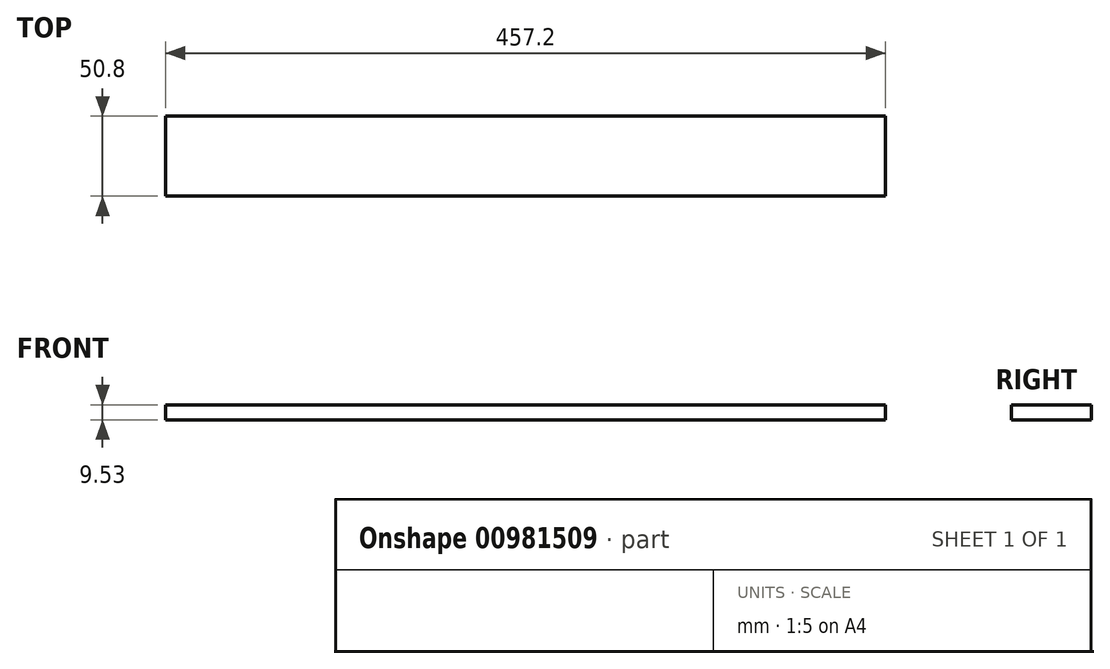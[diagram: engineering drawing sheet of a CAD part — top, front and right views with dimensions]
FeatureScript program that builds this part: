
annotation { "Feature Type Name" : "Feature", "Feature Type Description" : "" }
export const myFeature = defineFeature(function(context is Context, id is Id, definition is map)
    precondition{}
    {
        {
            var Q0;
            Q0=qCreatedBy(makeId("Top.planeOp"),FACE);
            var sketch = newSketch(context, id + "F0", { "sketchPlane" : qUnion([Q0])});
            skLineSegment(sketch, "E0.bottom", {"start": v(-224.33, 10.37) * mm, "end": v(232.87, 10.37) * mm});
            skLineSegment(sketch, "E0.top", {"start": v(-224.33, -40.43) * mm, "end": v(232.87, -40.43) * mm});
            skLineSegment(sketch, "E0.left", {"start": v(-224.33, 10.37) * mm, "end": v(-224.33, -40.43) * mm});
            skLineSegment(sketch, "E0.right", {"start": v(232.87, 10.37) * mm, "end": v(232.87, -40.43) * mm});
            skSolve(sketch);
        }
        {
            var Q0;
            Q0 = qSketchRegion(id + "F0", true);
            var Q1;
            Q1=makeQuery(id+"F0.imprint","IMPRINT",FACE,{"disambiguationData":[TD([[makeQuery(id+"F0.imprint","IMPRINT",EDGE,{"derivedFrom":sQuery(id+"F0.wireOp",EDGE,"E0.bottom")}),-1.0]])]});
            extrude(context, id + "F1", {"entities" : qUnion([Q0, Q1]), "depth" : 9.52 * mm, "offsetDistance" : 25.4 * mm});
        }
    });
